# Revit family: cadclips-dg-Glulam-Western Species
name_source: partatom
category: Structural Framing
revit_build: Autodesk Revit 2018 (Build: 20170927_1515(x64)
units: mm (PartAtom-declared; Revit-internal decimal feet)

## family parameters
Always export as geometry = No
Always vertical = Yes
Cut with Voids When Loaded = No
Material for Model Behavior = Wood
OmniClass Number = 23.25.30.11.14.14
OmniClass Title = Beams
Section Shape = Not Defined
Shared = No
Show family pre-cut in plan views = Yes
Structural Framing Length Roundoff = 0' - 0"

## types (3) — shared parameters
Assembly Code = B10

## per-type parameters (varying)
| type | A | Ix | Iy | Laminations | Sx | Sy | b | d |
| 5.125x15 | 76.88 in² | 1441 | 168.3 | 10 | 192.2 | 65.66 | 0' - 5 1/8" | 1' - 3" |
| 3.125x12 | 37.5 in² | 450 | 30.52 | 8 | 75 | 19.53 | 0' - 3 1/8" | 1' - 0" |
| 5.125x14 | 76.88 in² | 1441 | 168.3 | 10 | 192.2 | 65.66 | 0' - 5 1/8" | 1' - 2" |

## geometry (parser evidence)
native form markers: Sweep x2
no freeform markers — native parametric forms only
